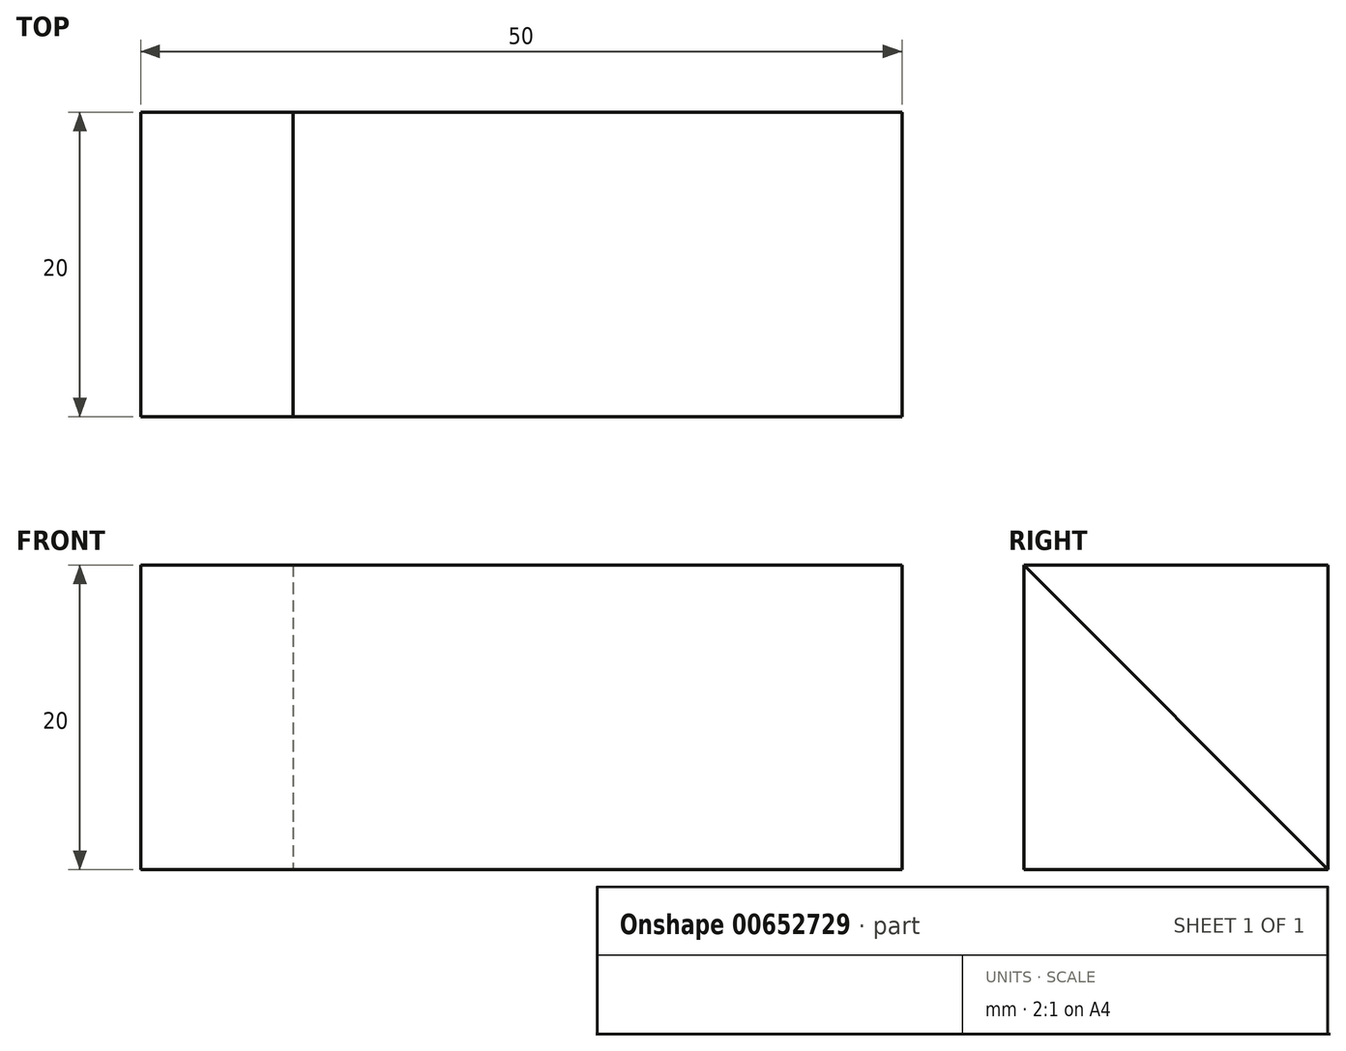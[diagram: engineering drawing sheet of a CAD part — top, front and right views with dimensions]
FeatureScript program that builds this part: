
annotation { "Feature Type Name" : "Feature", "Feature Type Description" : "" }
export const myFeature = defineFeature(function(context is Context, id is Id, definition is map)
    precondition{}
    {
        {
            var Q0;
            Q0=qCreatedBy(makeId("Top.planeOp"),FACE);
            var sketch = newSketch(context, id + "F0", { "sketchPlane" : qUnion([Q0])});
            skLineSegment(sketch, "E0.bottom", {"start": v(25, 10) * mm, "end": v(-25, 10) * mm});
            skLineSegment(sketch, "E0.top", {"start": v(25, -10) * mm, "end": v(-25, -10) * mm});
            skLineSegment(sketch, "E0.left", {"start": v(25, 10) * mm, "end": v(25, -10) * mm});
            skLineSegment(sketch, "E0.right", {"start": v(-25, 10) * mm, "end": v(-25, -10) * mm});
            skPoint(sketch, "E0.middle", {"position": v(0, 0) * mm});
            skSolve(sketch);
        }
        {
            var Q0;
            Q0=makeQuery(id+"F0.imprint","IMPRINT",FACE,{"disambiguationData":[TD([[makeQuery(id+"F0.imprint","IMPRINT",EDGE,{"derivedFrom":sQuery(id+"F0.wireOp",EDGE,"E0.bottom")}),1.0]])]});
            extrude(context, id + "F1", {"entities" : qUnion([Q0]), "depth" : 20 * mm, "offsetDistance" : 25 * mm});
        }
        {
            var Q0;
            Q0=makeQuery(id+"F1.opExtrude","SWEPT_FACE",FACE,{"disambiguationData":[OSD([sQuery(id+"F0.wireOp",EDGE,"E0.left")])]});
            var sketch = newSketch(context, id + "F2", { "sketchPlane" : qUnion([Q0])});
            skLineSegment(sketch, "E1", {"start": v(-10, 20) * mm, "end": v(10, 0) * mm});
            skLineSegment(sketch, "E2", {"start": v(10, 0) * mm, "end": v(-10, 0) * mm});
            skLineSegment(sketch, "E3", {"start": v(-10, 0) * mm, "end": v(-10, 20) * mm});
            skSolve(sketch);
        }
        {
            var Q0;
            Q0=makeQuery(id+"F2.imprint","IMPRINT",FACE,{"disambiguationData":[TD([[makeQuery(id+"F2.imprint","IMPRINT",EDGE,{"derivedFrom":sQuery(id+"F2.wireOp",EDGE,"E1")}),1.0]])]});
            extrude(context, id + "F3", {"entities" : qUnion([Q0]), "operationType" : NewBodyOperationType.REMOVE, "oppositeDirection" : true, "depth" : 40 * mm, "offsetDistance" : 25 * mm});
        }
        {
            var Q0;
            Q0=makeQuery(id+"F3.boolean.opBoolean","COPY",FACE,{"derivedFrom":makeQuery(id+"F3.opExtrude","SWEPT_FACE",FACE,{"disambiguationData":[OSD([sQuery(id+"F2.wireOp",EDGE,"E1")])]})});
            cPlane(context, id + "F4", {"entities" : qUnion([Q0]), "cplaneType" : CPlaneType.OFFSET, "offset" : 0 * mm, "oppositeDirection" : true, "width" : 150 * mm, "height" : 150 * mm});
        }
    });
